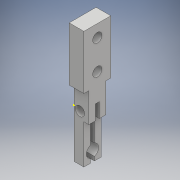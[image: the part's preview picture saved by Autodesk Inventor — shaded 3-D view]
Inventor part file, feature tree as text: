
AUTODESK INVENTOR PART (.ipt)
format: ipt  version: 2017 (Build 210142000, 142)  size: 162,304 bytes
history: native  units: mm
features: sketch x5, extrude x4
ambient origin geometry x8: Origin, YZ Plane, XZ Plane, XY Plane, X Axis, Y Axis, Z Axis, Center Point
bodies: Solid1 (feature_tree)
feature tree (9):
  extrude  "Extrusion1"  Depth=10.0mm
  extrude  "Extrusion2"  Depth=2.0mm
  sketch  "Sketch4"  dims[d10=8.0mm d11=3.0mm]
  extrude  "Extrusion3"  Depth=3.0mm
  extrude  "Extrusion4"  Depth=3.5mm TaperAngle=0.0deg
  sketch  "Sketch2"  dims[d0=10.0mm d1=10.0mm]
  sketch  "Sketch3"  dims[d2=2.0mm d9=1.9mm]
  sketch  "Sketch5"  dims[d12=1.8mm d13=3.5mm d14=0.0mm]
  sketch  "Sketch6"  dims[d15=2.5mm d16=2.0mm d17=0.4mm d18=11.0mm d19=0.8mm d20=10.0mm d21=0.0mm d22=3.0mm d23=1.0mm d24=1.0mm d25=3.0mm d26=0.0mm d27=5.0mm d28=2.75mm d32=1.9mm d33=2.5mm d34=1.9mm d35=6.0mm d36=3.0mm d37=0.0mm]
